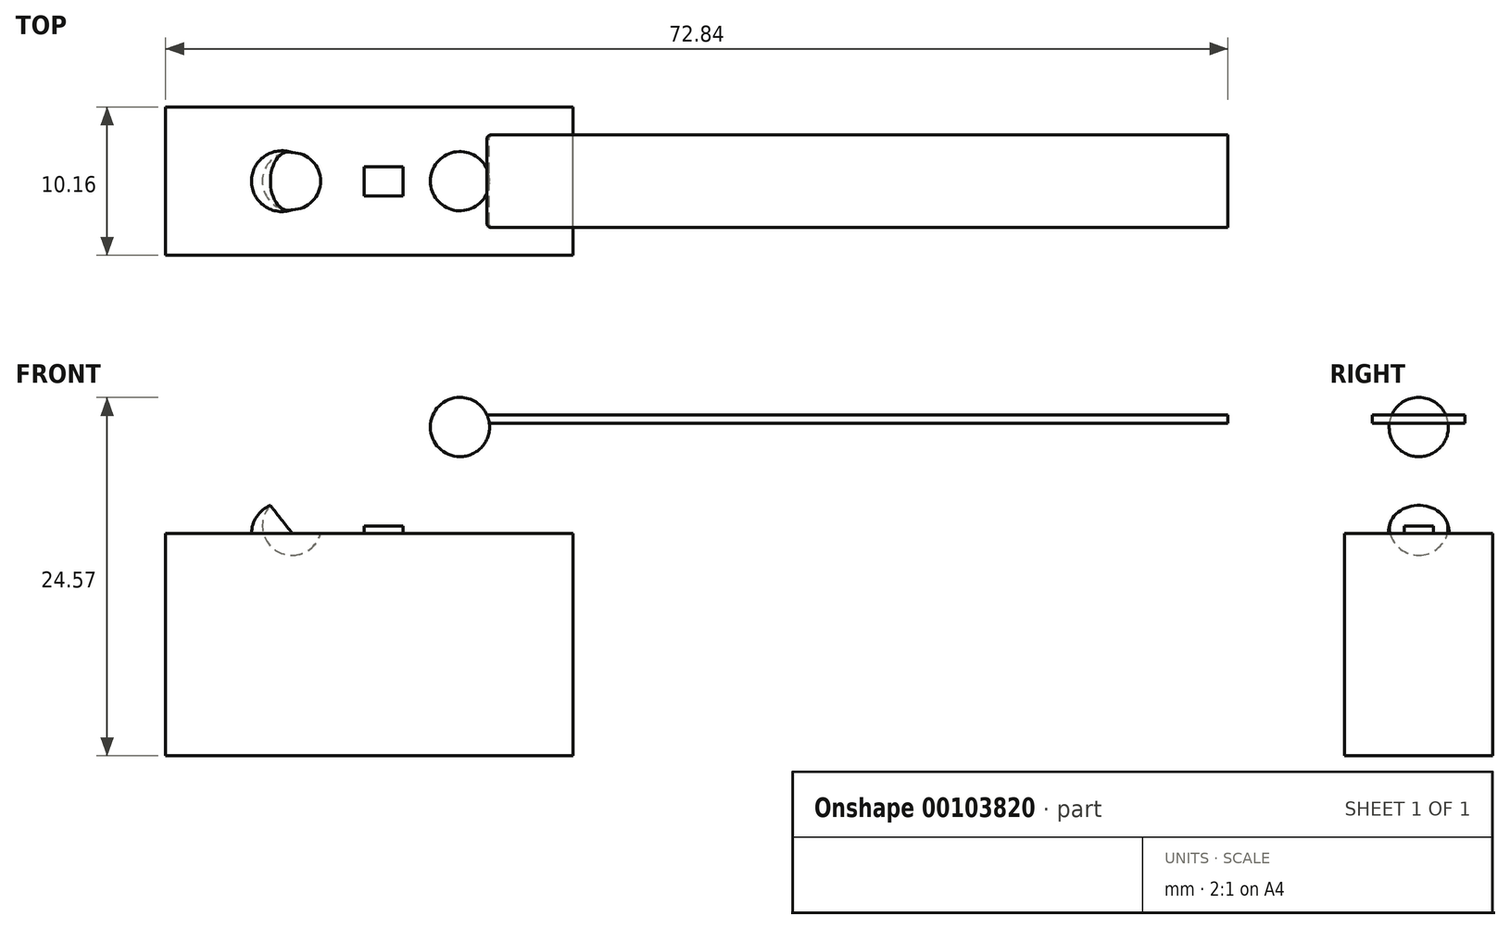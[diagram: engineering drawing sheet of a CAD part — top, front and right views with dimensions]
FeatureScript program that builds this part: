
annotation { "Feature Type Name" : "Feature", "Feature Type Description" : "" }
export const myFeature = defineFeature(function(context is Context, id is Id, definition is map)
    precondition{}
    {
        {
            var Q0;
            Q0=qCreatedBy(makeId("Front.planeOp"),FACE);
            var sketch = newSketch(context, id + "F0", { "sketchPlane" : qUnion([Q0])});
            skLineSegment(sketch, "E0.bottom", {"start": v(-19.48, 10.45) * mm, "end": v(-8.87, 10.45) * mm});
            skLineSegment(sketch, "E0.top", {"start": v(-19.48, -4.8) * mm, "end": v(8.46, -4.8) * mm});
            skLineSegment(sketch, "E0.left", {"start": v(-19.48, 10.45) * mm, "end": v(-19.48, -4.8) * mm});
            skLineSegment(sketch, "E0.right", {"start": v(8.46, 10.45) * mm, "end": v(8.46, -4.8) * mm});
            skLineSegment(sketch, "E1.bottom", {"start": v(-5.86, 10.45) * mm, "end": v(-3.2, 10.45) * mm});
            skLineSegment(sketch, "E1.top", {"start": v(-5.86, 10.95) * mm, "end": v(-3.2, 10.95) * mm});
            skLineSegment(sketch, "E1.left", {"start": v(-5.86, 10.45) * mm, "end": v(-5.86, 10.95) * mm});
            skLineSegment(sketch, "E1.right", {"start": v(-3.2, 10.45) * mm, "end": v(-3.2, 10.95) * mm});
            skLineSegment(sketch, "E2.trimOffspring", {"start": v(-7.54, 10.45) * mm, "end": v(8.46, 10.45) * mm});
            skLineSegment(sketch, "E3", {"start": v(-8.87, 10.45) * mm, "end": v(-7.54, 10.45) * mm});
            skCircle(sketch, "E4", {"center": v(-11.5, 10.45) * mm, "radius": 2.08 * mm});
            skSolve(sketch);
        }
        {
            var Q0;
            Q0=makeQuery(id+"F0.imprint","IMPRINT",FACE,{"disambiguationData":[TD([[makeQuery(id+"F0.imprint","IMPRINT",EDGE,{"derivedFrom":sQuery(id+"F0.wireOp",EDGE,"E0.top")}),1.0]])]});
            var Q1;
            {var subQ0=sQuery(id+"F0.wireOp",EDGE,"BpK1UfCY-Wrev-3VUj-3O45-5ofnMJrVSKVC");var subQ1=sQuery(id+"F0.wireOp",EDGE,"E0.bottom");var subQ2=makeQuery(id+"F0.imprint","INTERSECT",VERTEX,{"disambiguationData":[OD(0.0)],"derivedFrom":[subQ1,subQ0]});Q1=makeQuery(id+"F0.imprint","IMPRINT",FACE,{"disambiguationData":[TD([[makeQuery(id+"F0.imprint","IMPRINT",EDGE,{"disambiguationData":[TD([[subQ2,-1.0]])],"derivedFrom":subQ1}),-1.0]])]});}
            var Q2;
            {var subQ0=sQuery(id+"F0.wireOp",EDGE,"8nkgdPqc-b5RA-ZGjc-Yj6Y-uAEL0VMT7Qx2");var subQ1=sQuery(id+"F0.wireOp",EDGE,"E0.bottom");var subQ2=makeQuery(id+"F0.imprint","INTERSECT",VERTEX,{"disambiguationData":[OD(0.0)],"derivedFrom":[subQ1,subQ0]});Q2=makeQuery(id+"F0.imprint","IMPRINT",FACE,{"disambiguationData":[TD([[makeQuery(id+"F0.imprint","IMPRINT",EDGE,{"disambiguationData":[TD([[subQ2,1.0]])],"derivedFrom":subQ1}),-1.0]])]});}
            var Q3;
            {var subQ0=sQuery(id+"F0.wireOp",EDGE,"8nkgdPqc-b5RA-ZGjc-Yj6Y-uAEL0VMT7Qx2");var subQ1=sQuery(id+"F0.wireOp",EDGE,"E0.bottom");var subQ2=makeQuery(id+"F0.imprint","INTERSECT",VERTEX,{"disambiguationData":[OD(1.0)],"derivedFrom":[subQ1,subQ0]});Q3=makeQuery(id+"F0.imprint","IMPRINT",FACE,{"disambiguationData":[TD([[makeQuery(id+"F0.imprint","IMPRINT",EDGE,{"disambiguationData":[TD([[subQ2,-1.0]])],"derivedFrom":subQ1}),-1.0]])]});}
            extrude(context, id + "F1", {"entities" : qUnion([Q0, Q1, Q2, Q3]), "endBound" : BoundingType.SYMMETRIC, "depth" : 10.16 * mm});
        }
        {
            var Q0;
            {var subQ0=sQuery(id+"F0.wireOp",EDGE,"BpK1UfCY-Wrev-3VUj-3O45-5ofnMJrVSKVC");var subQ1=sQuery(id+"F0.wireOp",EDGE,"E0.bottom");var subQ2=makeQuery(id+"F0.imprint","INTERSECT",VERTEX,{"disambiguationData":[OD(0.0)],"derivedFrom":[subQ1,subQ0]});Q0=makeQuery(id+"F0.imprint","IMPRINT",FACE,{"disambiguationData":[TD([[makeQuery(id+"F0.imprint","IMPRINT",EDGE,{"disambiguationData":[TD([[subQ2,-1.0]])],"derivedFrom":subQ1}),1.0]])]});}
            var Q1;
            {var subQ0=sQuery(id+"F0.wireOp",EDGE,"8nkgdPqc-b5RA-ZGjc-Yj6Y-uAEL0VMT7Qx2");var subQ1=sQuery(id+"F0.wireOp",EDGE,"E0.bottom");var subQ2=makeQuery(id+"F0.imprint","INTERSECT",VERTEX,{"disambiguationData":[OD(1.0)],"derivedFrom":[subQ1,subQ0]});Q1=makeQuery(id+"F0.imprint","IMPRINT",FACE,{"disambiguationData":[TD([[makeQuery(id+"F0.imprint","IMPRINT",EDGE,{"disambiguationData":[TD([[subQ2,-1.0]])],"derivedFrom":subQ1}),1.0]])]});}
            var Q2;
            Q2=sQuery(id+"F0.wireOp",EDGE,"E0.bottom");
            revolve(context, id + "F2", {"operationType" : NewBodyOperationType.ADD, "entities" : qUnion([Q0, Q1]), "axis" : qUnion([Q2]), "revolveType" : RevolveType.FULL});
        }
        {
            var Q0;
            Q0=qCreatedBy(makeId("Front.planeOp"),FACE);
            var sketch = newSketch(context, id + "F3", { "sketchPlane" : qUnion([Q0])});
            skCircle(sketch, "E5", {"center": v(-10.8, 10.99) * mm, "radius": 2.03 * mm});
            skLineSegment(sketch, "E6", {"start": v(-10.8, 8.96) * mm, "end": v(-10.8, 13.02) * mm});
            skSolve(sketch);
        }
        {
            var Q0;
            Q0=makeQuery(id+"F0.imprint","IMPRINT",FACE,{"disambiguationData":[TD([[makeQuery(id+"F0.imprint","IMPRINT",EDGE,{"derivedFrom":sQuery(id+"F0.wireOp",EDGE,"E1.top")}),-1.0]])]});
            extrude(context, id + "F4", {"entities" : qUnion([Q0]), "endBound" : BoundingType.SYMMETRIC, "depth" : 2 * mm});
        }
        {
            var Q0;
            {var subQ0=sQuery(id+"F3.wireOp",EDGE,"E6");Q0=makeQuery(id+"F3.imprint","IMPRINT",FACE,{"disambiguationData":[TD([[makeQuery(id+"F3.imprint","IMPRINT",EDGE,{"derivedFrom":subQ0}),-1.0]])]});}
            var Q1;
            Q1=sQuery(id+"F3.wireOp",EDGE,"E6");
            revolve(context, id + "F5", {"operationType" : NewBodyOperationType.REMOVE, "entities" : qUnion([Q0]), "axis" : qUnion([Q1]), "revolveType" : RevolveType.FULL, "oppositeDirection" : true});
        }
        {
            var Q0;
            Q0=qCreatedBy(makeId("Front.planeOp"),FACE);
            var sketch = newSketch(context, id + "F6", { "sketchPlane" : qUnion([Q0])});
            skCircle(sketch, "E7", {"center": v(0.7, 17.75) * mm, "radius": 2.03 * mm});
            skLineSegment(sketch, "E8", {"start": v(2.56, 18.57) * mm, "end": v(53.36, 18.57) * mm});
            skLineSegment(sketch, "E9", {"start": v(53.36, 18.57) * mm, "end": v(53.36, 18.02) * mm});
            skLineSegment(sketch, "E10", {"start": v(53.36, 18.02) * mm, "end": v(2.72, 18.02) * mm});
            skLineSegment(sketch, "E11", {"start": v(0.7, 19.78) * mm, "end": v(0.7, 15.72) * mm});
            skSolve(sketch);
        }
        {
            var Q0;
            {var subQ0=sQuery(id+"F6.wireOp",EDGE,"E11");Q0=makeQuery(id+"F6.imprint","IMPRINT",FACE,{"disambiguationData":[TD([[makeQuery(id+"F6.imprint","IMPRINT",EDGE,{"derivedFrom":subQ0}),-1.0]])]});}
            var Q1;
            Q1=sQuery(id+"F6.wireOp",EDGE,"E11");
            revolve(context, id + "F7", {"entities" : qUnion([Q0]), "axis" : qUnion([Q1]), "revolveType" : RevolveType.FULL});
        }
        {
            var Q0;
            {var subQ0=sQuery(id+"F6.wireOp",EDGE,"E8");Q0=makeQuery(id+"F6.imprint","IMPRINT",FACE,{"disambiguationData":[TD([[makeQuery(id+"F6.imprint","IMPRINT",EDGE,{"derivedFrom":subQ0}),-1.0]])]});}
            extrude(context, id + "F8", {"entities" : qUnion([Q0]), "endBound" : BoundingType.SYMMETRIC, "depth" : 6.35 * mm});
        }
        {
            var Q0;
            Q0=makeQuery(id+"F8.opExtrude","CAP_EDGE",EDGE,{"disambiguationData":[OSD([sQuery(id+"F6.wireOp",EDGE,"E7")])],"isStart":false});
            fillet(context, id + "F9", {"entities" : qUnion([Q0]), "radius" : 0.25 * mm, "tangentPropagation" : true, "allowEdgeOverflow" : false});
        }
        {
            var Q0;
            Q0=makeQuery(id+"F8.opExtrude","CAP_EDGE",EDGE,{"disambiguationData":[OSD([sQuery(id+"F6.wireOp",EDGE,"E7")])],"isStart":true});
            fillet(context, id + "F10", {"entities" : qUnion([Q0]), "radius" : 0.25 * mm, "tangentPropagation" : true, "allowEdgeOverflow" : false});
        }
    });
